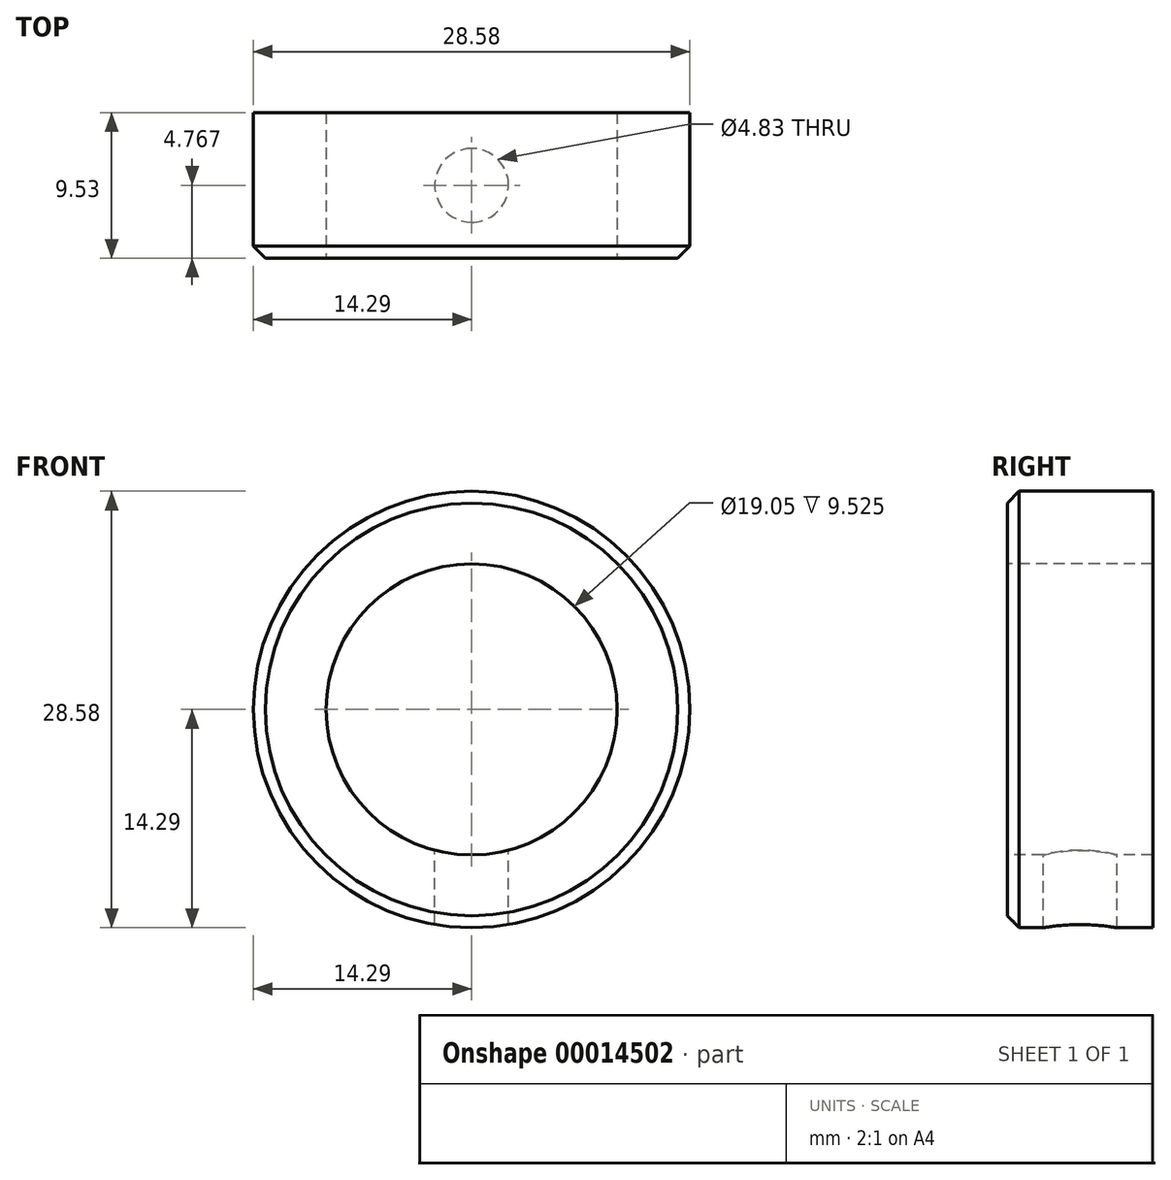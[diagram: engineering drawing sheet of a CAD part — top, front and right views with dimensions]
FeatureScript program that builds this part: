
annotation { "Feature Type Name" : "Feature", "Feature Type Description" : "" }
export const myFeature = defineFeature(function(context is Context, id is Id, definition is map)
    precondition{}
    {
        {
            var Q0;
            Q0=qCreatedBy(makeId("Front.planeOp"),FACE);
            var sketch = newSketch(context, id + "F0", { "sketchPlane" : qUnion([Q0])});
            skCircle(sketch, "E0", {"center": v(0, 0) * mm, "radius": 14.29 * mm});
            skSolve(sketch);
        }
        {
            var Q0;
            Q0=makeQuery(id+"F0.imprint","IMPRINT",FACE,{"disambiguationData":[TD([[makeQuery(id+"F0.imprint","IMPRINT",EDGE,{"derivedFrom":sQuery(id+"F0.wireOp",EDGE,"E0")}),1.0]])]});
            extrude(context, id + "F1", {"entities" : qUnion([Q0]), "depth" : 9.52 * mm});
        }
        {
            var Q0;
            Q0=makeQuery(id+"F1.opExtrude","CAP_FACE",FACE,{"disambiguationData":[OSD([sQuery(id+"F0.wireOp",EDGE,"E0")])],"isStart":false});
            var sketch = newSketch(context, id + "F2", { "sketchPlane" : qUnion([Q0])});
            skCircle(sketch, "E1", {"center": v(0, 0) * mm, "radius": 9.53 * mm});
            skSolve(sketch);
        }
        {
            var Q0;
            Q0=makeQuery(id+"F2.imprint","IMPRINT",FACE,{"disambiguationData":[TD([[makeQuery(id+"F2.imprint","IMPRINT",EDGE,{"derivedFrom":sQuery(id+"F2.wireOp",EDGE,"E1")}),1.0]])]});
            extrude(context, id + "F3", {"entities" : qUnion([Q0]), "operationType" : NewBodyOperationType.REMOVE, "endBound" : BoundingType.UP_TO_NEXT, "oppositeDirection" : true, "depth" : 25.4 * mm});
        }
        {
            var Q0;
            Q0=qCreatedBy(makeId("Top.planeOp"),FACE);
            var sketch = newSketch(context, id + "F4", { "sketchPlane" : qUnion([Q0])});
            skCircle(sketch, "E2", {"center": v(0, -4.76) * mm, "radius": 2.41 * mm});
            skSolve(sketch);
        }
        {
            var Q0;
            Q0 = qSketchRegion(id + "F4", true);
            extrude(context, id + "F5", {"entities" : qUnion([Q0]), "operationType" : NewBodyOperationType.REMOVE, "oppositeDirection" : true, "depth" : 25.4 * mm});
        }
        {
            var Q0;
            Q0=makeQuery(id+"F1.opExtrude","CAP_EDGE",EDGE,{"disambiguationData":[OSD([sQuery(id+"F0.wireOp",EDGE,"E0")])],"isStart":false});
            chamfer(context, id + "F6", {"entities" : qUnion([Q0]), "chamferType" : ChamferType.OFFSET_ANGLE, "width" : 0.79 * mm, "oppositeDirection" : false, "angle" : 45 * degree, "tangentPropagation" : true});
        }
    });
